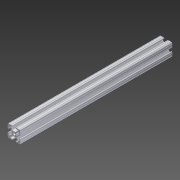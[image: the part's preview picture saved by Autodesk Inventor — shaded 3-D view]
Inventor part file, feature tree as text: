
AUTODESK INVENTOR PART (.ipt)
format: ipt  version: 2013 (Build 170138000, 138)  size: 163,840 bytes
history: native  units: in
note: dims shown in document units (in); Inventor stores cm internally (conversion verified against a paired STEP export)
features: extrude x1, imported_body x1
ambient origin geometry x8: Origin, YZ Plane, XZ Plane, XY Plane, X Axis, Y Axis, Z Axis, Center Point
feature tree (2):
  extrude  "Extrude1"  [1 undecoded]
  imported_body  "Base1"
note: 1 required parameter value undecoded (feature->parameter linkage not recoverable at this tier; creation-order binding heuristic only, values carry confidence <= 0.55)
